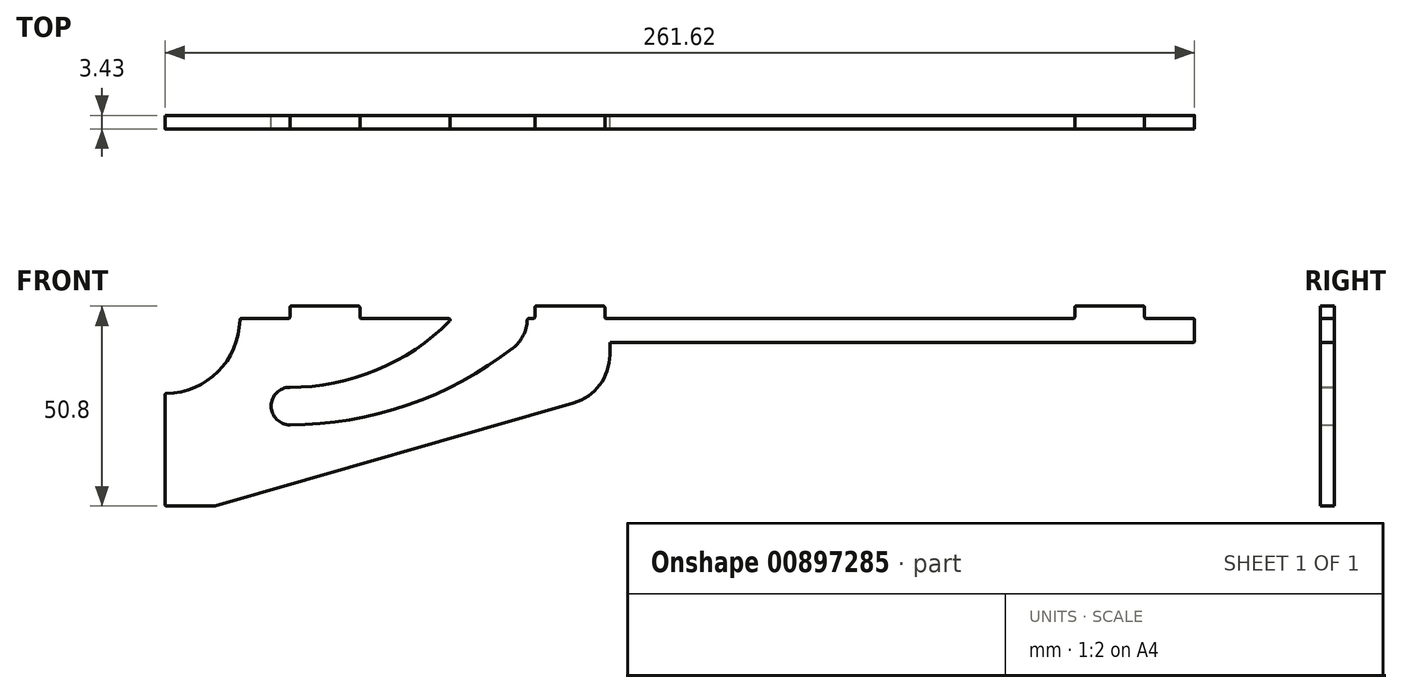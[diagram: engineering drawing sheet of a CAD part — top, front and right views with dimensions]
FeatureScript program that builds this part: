
annotation { "Feature Type Name" : "Feature", "Feature Type Description" : "" }
export const myFeature = defineFeature(function(context is Context, id is Id, definition is map)
    precondition{}
    {
        {
            var Q0;
            Q0=qCreatedBy(makeId("Front.planeOp"),FACE);
            var sketch = newSketch(context, id + "F0", { "sketchPlane" : qUnion([Q0])});
            skArc(sketch, "E0", {"start": v(-523.3, 351.65) * mm, "mid": v(-528.07, 346.89) * mm, "end": v(-523.3, 342.13) * mm});
            skArc(sketch, "E1", {"start": v(-523.3, 342.13) * mm, "mid": v(-493.35, 347.13) * mm, "end": v(-466.65, 361.6) * mm});
            skArc(sketch, "E2", {"start": v(-466.65, 361.6) * mm, "mid": v(-463.95, 364.93) * mm, "end": v(-462.98, 369.11) * mm});
            skLineSegment(sketch, "E3", {"start": v(-461.08, 369.11) * mm, "end": v(-462.98, 369.11) * mm});
            skLineSegment(sketch, "E4", {"start": v(-461.08, 372.29) * mm, "end": v(-461.08, 369.11) * mm});
            skLineSegment(sketch, "E5", {"start": v(-443.3, 372.29) * mm, "end": v(-461.08, 372.29) * mm});
            skLineSegment(sketch, "E6", {"start": v(-443.3, 369.11) * mm, "end": v(-443.3, 372.29) * mm});
            skLineSegment(sketch, "E7", {"start": v(-323.92, 369.11) * mm, "end": v(-443.3, 369.11) * mm});
            skLineSegment(sketch, "E8", {"start": v(-323.92, 372.29) * mm, "end": v(-323.92, 369.11) * mm});
            skLineSegment(sketch, "E9", {"start": v(-293.44, 363.02) * mm, "end": v(-293.44, 369.11) * mm});
            skLineSegment(sketch, "E10", {"start": v(-442.03, 363.02) * mm, "end": v(-293.44, 363.02) * mm});
            skLineSegment(sketch, "E11", {"start": v(-442.03, 359.88) * mm, "end": v(-442.03, 363.02) * mm});
            skArc(sketch, "E12", {"start": v(-451.22, 347.68) * mm, "mid": v(-444.58, 352.24) * mm, "end": v(-442.03, 359.88) * mm});
            skLineSegment(sketch, "E13", {"start": v(-542.36, 321.49) * mm, "end": v(-451.22, 347.68) * mm});
            skLineSegment(sketch, "E14", {"start": v(-555.06, 321.49) * mm, "end": v(-542.36, 321.49) * mm});
            skLineSegment(sketch, "E15", {"start": v(-555.06, 350.06) * mm, "end": v(-555.06, 321.49) * mm});
            skArc(sketch, "E16", {"start": v(-555.06, 350.06) * mm, "mid": v(-541.59, 355.64) * mm, "end": v(-536, 369.11) * mm});
            skLineSegment(sketch, "E17", {"start": v(-523.3, 369.11) * mm, "end": v(-536, 369.11) * mm});
            skLineSegment(sketch, "E18", {"start": v(-523.3, 372.29) * mm, "end": v(-523.3, 369.11) * mm});
            skLineSegment(sketch, "E19", {"start": v(-505.53, 372.29) * mm, "end": v(-523.3, 372.29) * mm});
            skLineSegment(sketch, "E20", {"start": v(-505.53, 369.11) * mm, "end": v(-505.53, 372.29) * mm});
            skLineSegment(sketch, "E21", {"start": v(-482.03, 369.11) * mm, "end": v(-505.53, 369.11) * mm});
            skArc(sketch, "E22", {"start": v(-523.3, 351.65) * mm, "mid": v(-500.9, 356.2) * mm, "end": v(-482.03, 369.11) * mm});
            skLineSegment(sketch, "E23", {"start": v(-306.14, 369.11) * mm, "end": v(-306.14, 372.29) * mm});
            skLineSegment(sketch, "E24", {"start": v(-293.44, 369.11) * mm, "end": v(-306.14, 369.11) * mm});
            skLineSegment(sketch, "E25", {"start": v(-306.14, 372.29) * mm, "end": v(-323.92, 372.29) * mm});
            skSolve(sketch);
        }
        {
            var Q0;
            Q0 = qSketchRegion(id + "F0", true);
            extrude(context, id + "F1", {"entities" : qUnion([Q0]), "depth" : 3.43 * mm, "offsetDistance" : 25.4 * mm});
        }
        {
            var Q0;
            Q0=makeQuery(id+"F1.opExtrude","SWEPT_EDGE",EDGE,{"disambiguationData":[OSD([sQuery(id+"F0.wireOp",EDGE,"E21"),sQuery(id+"F0.wireOp",EDGE,"E22")])]});
            var Q1;
            Q1=makeQuery(id+"F1.opExtrude","SWEPT_EDGE",EDGE,{"disambiguationData":[OSD([sQuery(id+"F0.wireOp",EDGE,"E4"),sQuery(id+"F0.wireOp",EDGE,"E5")])]});
            var Q2;
            Q2=makeQuery(id+"F1.opExtrude","SWEPT_EDGE",EDGE,{"disambiguationData":[OSD([sQuery(id+"F0.wireOp",EDGE,"E3"),sQuery(id+"F0.wireOp",EDGE,"E4")])]});
            var Q3;
            Q3=makeQuery(id+"F1.opExtrude","SWEPT_EDGE",EDGE,{"disambiguationData":[OSD([sQuery(id+"F0.wireOp",EDGE,"E2"),sQuery(id+"F0.wireOp",EDGE,"E3")])]});
            var Q4;
            Q4=makeQuery(id+"F1.opExtrude","SWEPT_EDGE",EDGE,{"disambiguationData":[OSD([sQuery(id+"F0.wireOp",EDGE,"E19"),sQuery(id+"F0.wireOp",EDGE,"E20")])]});
            var Q5;
            Q5=makeQuery(id+"F1.opExtrude","SWEPT_EDGE",EDGE,{"disambiguationData":[OSD([sQuery(id+"F0.wireOp",EDGE,"E18"),sQuery(id+"F0.wireOp",EDGE,"E19")])]});
            var Q6;
            Q6=makeQuery(id+"F1.opExtrude","SWEPT_EDGE",EDGE,{"disambiguationData":[OSD([sQuery(id+"F0.wireOp",EDGE,"E17"),sQuery(id+"F0.wireOp",EDGE,"E18")])]});
            var Q7;
            Q7=makeQuery(id+"F1.opExtrude","SWEPT_EDGE",EDGE,{"disambiguationData":[OSD([sQuery(id+"F0.wireOp",EDGE,"E16"),sQuery(id+"F0.wireOp",EDGE,"E17")])]});
            var Q8;
            Q8=makeQuery(id+"F1.opExtrude","SWEPT_EDGE",EDGE,{"disambiguationData":[OSD([sQuery(id+"F0.wireOp",EDGE,"E20"),sQuery(id+"F0.wireOp",EDGE,"E21")])]});
            var Q9;
            Q9=makeQuery(id+"F1.opExtrude","SWEPT_EDGE",EDGE,{"disambiguationData":[OSD([sQuery(id+"F0.wireOp",EDGE,"E15"),sQuery(id+"F0.wireOp",EDGE,"E16")])]});
            var Q10;
            Q10=makeQuery(id+"F1.opExtrude","SWEPT_EDGE",EDGE,{"disambiguationData":[OSD([sQuery(id+"F0.wireOp",EDGE,"E6"),sQuery(id+"F0.wireOp",EDGE,"E7")])]});
            var Q11;
            Q11=makeQuery(id+"F1.opExtrude","SWEPT_EDGE",EDGE,{"disambiguationData":[OSD([sQuery(id+"F0.wireOp",EDGE,"E5"),sQuery(id+"F0.wireOp",EDGE,"E6")])]});
            var Q12;
            Q12=makeQuery(id+"F1.opExtrude","SWEPT_EDGE",EDGE,{"disambiguationData":[OSD([sQuery(id+"F0.wireOp",EDGE,"E8"),sQuery(id+"F0.wireOp",EDGE,"E25")])]});
            var Q13;
            Q13=makeQuery(id+"F1.opExtrude","SWEPT_EDGE",EDGE,{"disambiguationData":[OSD([sQuery(id+"F0.wireOp",EDGE,"E23"),sQuery(id+"F0.wireOp",EDGE,"E25")])]});
            var Q14;
            Q14=makeQuery(id+"F1.opExtrude","SWEPT_EDGE",EDGE,{"disambiguationData":[OSD([sQuery(id+"F0.wireOp",EDGE,"E23"),sQuery(id+"F0.wireOp",EDGE,"E24")])]});
            var Q15;
            Q15=makeQuery(id+"F1.opExtrude","SWEPT_EDGE",EDGE,{"disambiguationData":[OSD([sQuery(id+"F0.wireOp",EDGE,"E7"),sQuery(id+"F0.wireOp",EDGE,"E8")])]});
            var Q16;
            Q16=makeQuery(id+"F1.opExtrude","SWEPT_EDGE",EDGE,{"disambiguationData":[OSD([sQuery(id+"F0.wireOp",EDGE,"E9"),sQuery(id+"F0.wireOp",EDGE,"E24")])]});
            var Q17;
            Q17=makeQuery(id+"F1.opExtrude","SWEPT_EDGE",EDGE,{"disambiguationData":[OSD([sQuery(id+"F0.wireOp",EDGE,"E9"),sQuery(id+"F0.wireOp",EDGE,"E10")])]});
            var Q18;
            Q18=makeQuery(id+"F1.opExtrude","SWEPT_EDGE",EDGE,{"disambiguationData":[OSD([sQuery(id+"F0.wireOp",EDGE,"E13"),sQuery(id+"F0.wireOp",EDGE,"E14")])]});
            var Q19;
            Q19=makeQuery(id+"F1.opExtrude","SWEPT_EDGE",EDGE,{"disambiguationData":[OSD([sQuery(id+"F0.wireOp",EDGE,"E14"),sQuery(id+"F0.wireOp",EDGE,"E15")])]});
            fillet(context, id + "F2", {"entities" : qUnion([Q0, Q1, Q2, Q3, Q4, Q5, Q6, Q7, Q8, Q9, Q10, Q11, Q12, Q13, Q14, Q15, Q16, Q17, Q18, Q19]), "radius" : 0.38 * mm, "tangentPropagation" : true, "allowEdgeOverflow" : false});
        }
    });
